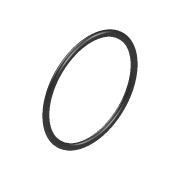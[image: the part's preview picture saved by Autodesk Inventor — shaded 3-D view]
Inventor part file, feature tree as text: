
AUTODESK INVENTOR PART (.ipt)
format: ipt  version: 2022.3 (Build 263350000, 350)  size: 134,656 bytes
history: native  units: mm
features: sketch x2, other x1, sweep x1
ambient origin geometry x8: Origin, YZ Plane, XZ Plane, XY Plane, X Axis, Y Axis, Z Axis, Center Point
bodies: Body1 (feature_tree)
feature tree (4):
  other  "Sólido1"
  sweep  "Barrido1"
  sketch  "Boceto1"  dims[d0=1.0mm d1=1.2mm]
  sketch  "Boceto2"  dims[d2=19.8mm d3=0.0mm d4=0.0mm]
